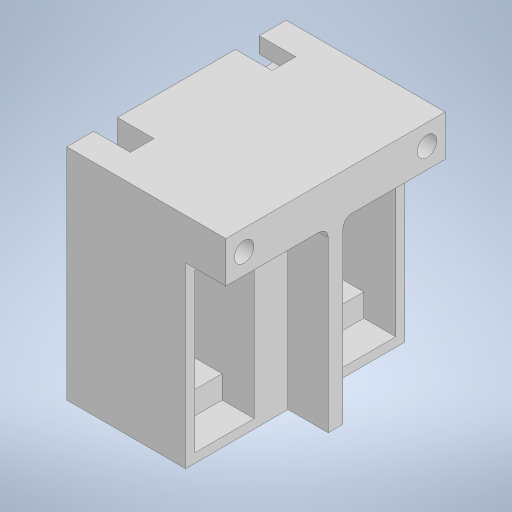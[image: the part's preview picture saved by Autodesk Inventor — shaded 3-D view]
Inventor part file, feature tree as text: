
AUTODESK INVENTOR PART (.ipt)
format: ipt  version: 2023 (Build 270158000, 158)  size: 340,480 bytes
history: native  units: in
note: dims shown in document units (in); Inventor stores cm internally (conversion verified against a paired STEP export)
features: extrude x9, sketch x8, projected_geometry x7, mirror x3
ambient origin geometry x8: Origin, YZ Plane, XZ Plane, XY Plane, X Axis, Y Axis, Z Axis, Center Point
bodies: Solid1 (feature_tree)
feature tree (27):
  extrude  "Extrusion1"  Depth=3.0in
  extrude  "Extrusion2"  Depth=1.5in
  extrude  "Extrusion3"  Depth=1.5625in TaperAngle=0.0deg
  extrude  "Extrusion4"  Depth=0.4375in TaperAngle=0.0deg
  mirror  "Mirror1"
  extrude  "Extrusion5"  Depth=0.1in
  extrude  "Extrusion6"  Depth=0.55in TaperAngle=0.0deg
  extrude  "Extrusion7"  Depth=2.4375in TaperAngle=0.0deg
  mirror  "Mirror2"
  extrude  "Extrusion8"  Depth=0.125in
  mirror  "Mirror3"
  extrude  "Extrusion10"  Depth=0.5625in TaperAngle=0.0deg
  sketch  "Sketch1"  dims[d0=3.0in d1=3.0in]
  sketch  "Sketch2"  dims[d2=1.5in d3=1.5in]
  sketch  "Sketch3"  dims[d4=1.625in d5=0.0in d13=1.5625in d14=0.0in]
  sketch  "Sketch4"  dims[d24=0.4375in d25=0.0in d34=1.5in d35=0.0in]
  projected_geometry  "Projected Loop4"
  projected_geometry  "Projected Loop5"
  sketch  "Sketch6"  dims[d36=0.2in d39=0.1in]
  sketch  "Sketch7"  dims[d40=0.125in d41=0.55in d42=0.0in]
  projected_geometry  "Projected Loop6"
  sketch  "Sketch8"  dims[d43=2.4375in d44=2.4375in d45=1.0in d46=0.0in]
  projected_geometry  "Projected Loop9"
  projected_geometry  "Projected Loop10"
  projected_geometry  "Projected Loop11"
  sketch  "Sketch11"  dims[d49=0.375in d50=0.125in d51=1.0in d52=0.0in d53=0.1902in d54=0.375in d55=0.0in d64=0.8125in d65=1.75in d66=0.125in d67=0.4375in d68=0.3125in d69=0.8125in d70=0.8125in d71=0.8125in d72=0.1in d73=0.325in d74=0.5in d75=0.8125in d76=0.4062in d77=2.5in d78=3.0in d79=1.25in d80=0.5625in d81=0.2812in d82=0.2812in d83=0.27in d84=0.27in d85=0.0in d86=0.0in]
  projected_geometry  "Projected Loop12"
